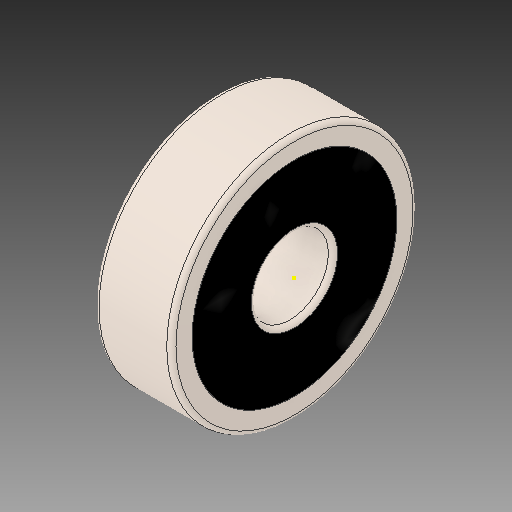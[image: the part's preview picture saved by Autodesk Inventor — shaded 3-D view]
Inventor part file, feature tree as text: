
AUTODESK INVENTOR PART (.ipt)
format: ipt  version: 2017 (Build 210142000, 142)  size: 2,295,808 bytes
history: imported  units: mm
features: other x22, sketch x3, imported_body x1
ambient origin geometry x8: Origin, YZ Plane, XZ Plane, XY Plane, X Axis, Y Axis, Z Axis, Center Point
bodies: Solid1 (imported_parasolid), Solid2 (imported_parasolid), Solid3 (imported_parasolid), Solid4 (imported_parasolid), Solid5 (imported_parasolid), Solid6 (imported_parasolid), Solid7 (imported_parasolid), Solid8 (imported_parasolid), Solid9 (imported_parasolid), Solid10 (imported_parasolid), Solid11 (imported_parasolid), Solid12 (imported_parasolid), Solid13 (imported_parasolid), Solid14 (imported_parasolid), Solid15 (imported_parasolid), Solid16 (imported_parasolid), Solid17 (imported_parasolid), Solid18 (imported_parasolid), Solid19 (imported_parasolid), Solid20 (imported_parasolid)
feature tree (26):
  other  "SKF 625.ipt"
  other  "Solid1::SKF 625.ipt"
  other  "Solid2::SKF 625.ipt"
  other  "Solid3::SKF 625.ipt"
  other  "Solid4::SKF 625.ipt"
  other  "Solid5::SKF 625.ipt"
  other  "Solid6::SKF 625.ipt"
  other  "Solid7::SKF 625.ipt"
  other  "Solid8::SKF 625.ipt"
  other  "Solid9::SKF 625.ipt"
  other  "Solid10::SKF 625.ipt"
  other  "Solid11::SKF 625.ipt"
  other  "Solid12::SKF 625.ipt"
  other  "Solid13::SKF 625.ipt"
  other  "Solid14::SKF 625.ipt"
  other  "Solid15::SKF 625.ipt"
  other  "Solid16::SKF 625.ipt"
  other  "Solid17::SKF 625.ipt"
  other  "Solid18::SKF 625.ipt"
  other  "Solid19::SKF 625.ipt"
  other  "Solid20::SKF 625.ipt"
  other  "TaggingFeature1"
  sketch  "Sketch1"  dims[d0=10.0mm]
  sketch  "Sketch2"
  sketch  "Sketch3"
  imported_body  NMx_Import_Brep_tag  [imported B-rep: ~49 faces, bbox_mm=None]
